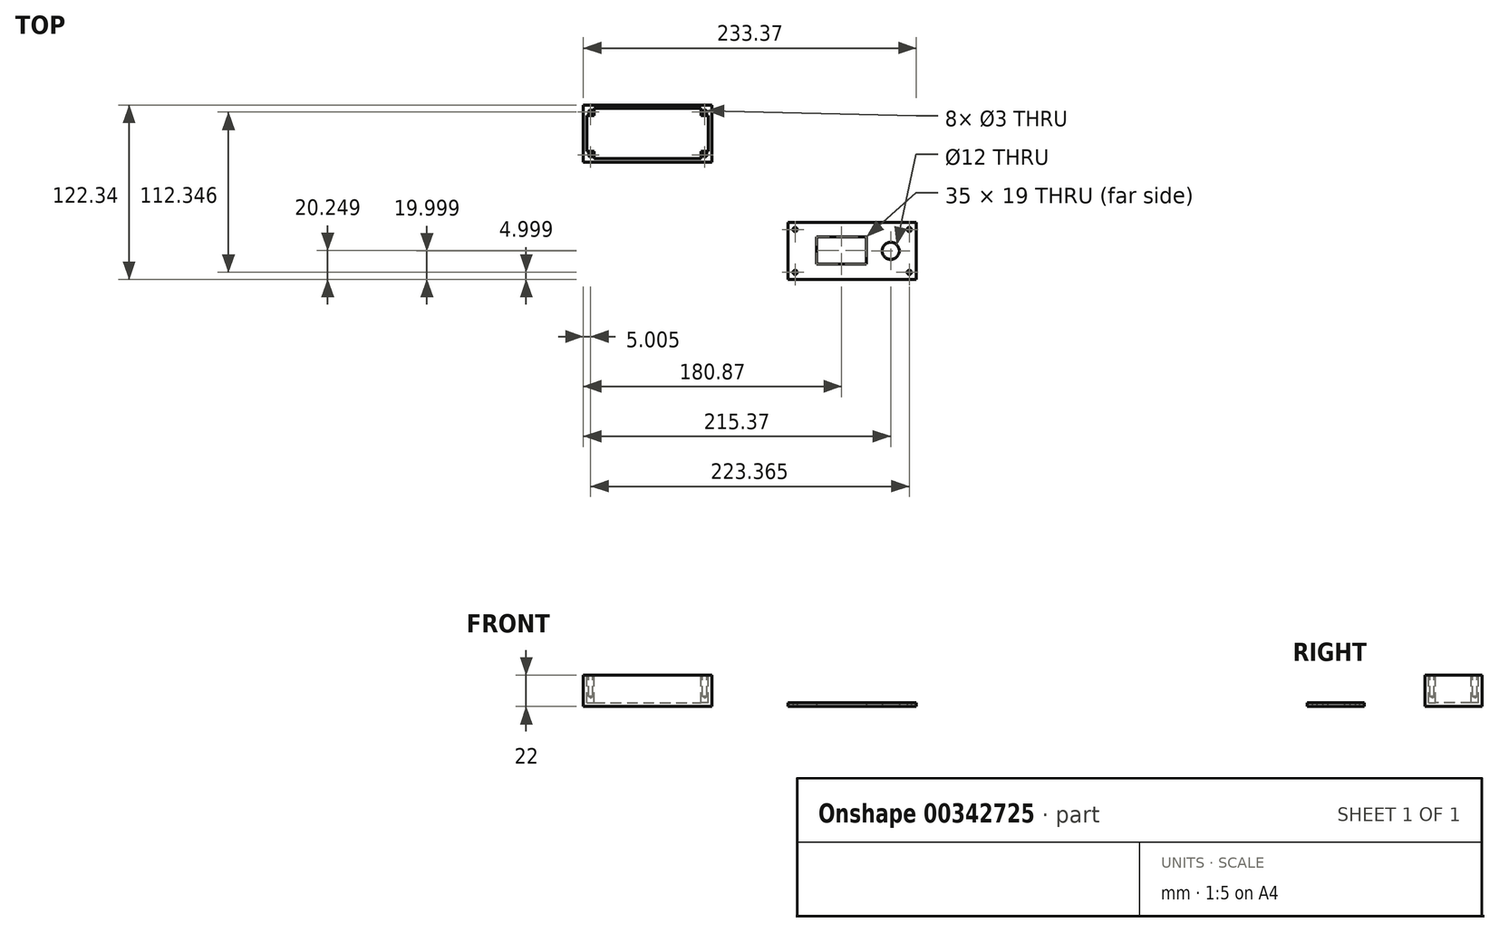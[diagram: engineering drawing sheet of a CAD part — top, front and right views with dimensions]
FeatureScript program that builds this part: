
annotation { "Feature Type Name" : "Feature", "Feature Type Description" : "" }
export const myFeature = defineFeature(function(context is Context, id is Id, definition is map)
    precondition{}
    {
        {
            var Q0;
            Q0=qCreatedBy(makeId("Top.planeOp"),FACE);
            var sketch = newSketch(context, id + "F0", { "sketchPlane" : qUnion([Q0])});
            skLineSegment(sketch, "E0.bottom", {"start": v(-186.8, 103.04) * mm, "end": v(-96.8, 103.04) * mm});
            skLineSegment(sketch, "E0.top", {"start": v(-186.8, 63.04) * mm, "end": v(-96.8, 63.04) * mm});
            skLineSegment(sketch, "E0.left", {"start": v(-186.8, 103.04) * mm, "end": v(-186.8, 63.04) * mm});
            skLineSegment(sketch, "E0.right", {"start": v(-96.8, 103.04) * mm, "end": v(-96.8, 63.04) * mm});
            skSolve(sketch);
        }
        {
            var Q0;
            Q0=makeQuery(id+"F0.imprint","IMPRINT",FACE,{"disambiguationData":[TD([[makeQuery(id+"F0.imprint","IMPRINT",EDGE,{"derivedFrom":sQuery(id+"F0.wireOp",EDGE,"E0.bottom")}),-1.0]])]});
            extrude(context, id + "F1", {"entities" : qUnion([Q0]), "depth" : 22 * mm});
        }
        {
            var Q0;
            Q0=makeQuery(id+"F1.opExtrude","CAP_FACE",FACE,{"disambiguationData":[OSD([sQuery(id+"F0.wireOp",EDGE,"E0.bottom"),sQuery(id+"F0.wireOp",EDGE,"E0.top"),sQuery(id+"F0.wireOp",EDGE,"E0.left"),sQuery(id+"F0.wireOp",EDGE,"E0.right")])],"isStart":false});
            shell(context, id + "F2", {"entities" : qUnion([Q0]), "thickness" : 2.5 * mm});
        }
        {
            var Q0;
            Q0=qCreatedBy(makeId("Top.planeOp"),FACE);
            var sketch = newSketch(context, id + "F3", { "sketchPlane" : qUnion([Q0])});
            skLineSegment(sketch, "E1.bottom", {"start": v(-43.44, 20.7) * mm, "end": v(46.56, 20.7) * mm});
            skLineSegment(sketch, "E1.top", {"start": v(-43.44, -19.3) * mm, "end": v(46.56, -19.3) * mm});
            skLineSegment(sketch, "E1.left", {"start": v(-43.44, 20.7) * mm, "end": v(-43.44, -19.3) * mm});
            skLineSegment(sketch, "E1.right", {"start": v(46.56, 20.7) * mm, "end": v(46.56, -19.3) * mm});
            skLineSegment(sketch, "E2.bottom", {"start": v(11.56, -8.55) * mm, "end": v(-23.44, -8.55) * mm});
            skLineSegment(sketch, "E2.top", {"start": v(11.56, 10.45) * mm, "end": v(-23.44, 10.45) * mm});
            skLineSegment(sketch, "E2.left", {"start": v(11.56, -8.55) * mm, "end": v(11.56, 10.45) * mm});
            skLineSegment(sketch, "E2.right", {"start": v(-23.44, -8.55) * mm, "end": v(-23.44, 10.45) * mm});
            skPoint(sketch, "E2.middle", {"position": v(-5.94, 0.95) * mm});
            skPoint(sketch, "E3", {"position": v(20.67, 0.11) * mm});
            skCircle(sketch, "E4", {"center": v(41.56, 15.7) * mm, "radius": 1.5 * mm});
            skCircle(sketch, "E5", {"center": v(41.56, -14.3) * mm, "radius": 1.5 * mm});
            skCircle(sketch, "E6", {"center": v(-38.44, 15.7) * mm, "radius": 1.5 * mm});
            skCircle(sketch, "E7", {"center": v(-38.44, -14.3) * mm, "radius": 1.5 * mm});
            skSolve(sketch);
        }
        {
            var Q0;
            Q0=makeQuery(id+"F3.imprint","IMPRINT",FACE,{"disambiguationData":[TD([[makeQuery(id+"F3.imprint","IMPRINT",EDGE,{"derivedFrom":sQuery(id+"F3.wireOp",EDGE,"E1.bottom")}),-1.0]])]});
            extrude(context, id + "F4", {"entities" : qUnion([Q0]), "depth" : 2.5 * mm});
        }
        {
            var Q0;
            Q0=makeQuery(id+"F3.imprint","IMPRINT",FACE,{"disambiguationData":[TD([[makeQuery(id+"F3.imprint","IMPRINT",EDGE,{"derivedFrom":sQuery(id+"F3.wireOp",EDGE,"E1.bottom")}),-1.0]])]});
            var sketch = newSketch(context, id + "F5", { "sketchPlane" : qUnion([Q0])});
            skCircle(sketch, "E8", {"center": v(28.56, 0.7) * mm, "radius": 6 * mm});
            skSolve(sketch);
        }
        {
            var Q0;
            Q0=makeQuery(id+"F5.imprint","IMPRINT",FACE,{"disambiguationData":[TD([[makeQuery(id+"F5.imprint","IMPRINT",EDGE,{"derivedFrom":sQuery(id+"F5.wireOp",EDGE,"E8")}),1.0]])]});
            extrude(context, id + "F6", {"entities" : qUnion([Q0]), "operationType" : NewBodyOperationType.REMOVE, "depth" : 25 * mm});
        }
        {
            var Q0;
            Q0=makeQuery(id+"F1.opExtrude","CAP_FACE",FACE,{"disambiguationData":[OSD([sQuery(id+"F0.wireOp",EDGE,"E0.bottom"),sQuery(id+"F0.wireOp",EDGE,"E0.top"),sQuery(id+"F0.wireOp",EDGE,"E0.left"),sQuery(id+"F0.wireOp",EDGE,"E0.right")])],"isStart":false});
            var sketch = newSketch(context, id + "F7", { "sketchPlane" : qUnion([Q0])});
            skLineSegment(sketch, "E9.bottom", {"start": v(-184.3, 95.54) * mm, "end": v(-179.3, 95.54) * mm});
            skLineSegment(sketch, "E9.top", {"start": v(-184.3, 100.54) * mm, "end": v(-179.3, 100.54) * mm});
            skLineSegment(sketch, "E9.left", {"start": v(-184.3, 95.54) * mm, "end": v(-184.3, 100.54) * mm});
            skLineSegment(sketch, "E9.right", {"start": v(-179.3, 95.54) * mm, "end": v(-179.3, 100.54) * mm});
            skLineSegment(sketch, "E10.bottom", {"start": v(-184.3, 65.54) * mm, "end": v(-179.3, 65.54) * mm});
            skLineSegment(sketch, "E10.top", {"start": v(-184.3, 70.54) * mm, "end": v(-179.3, 70.54) * mm});
            skLineSegment(sketch, "E10.left", {"start": v(-184.3, 65.54) * mm, "end": v(-184.3, 70.54) * mm});
            skLineSegment(sketch, "E10.right", {"start": v(-179.3, 65.54) * mm, "end": v(-179.3, 70.54) * mm});
            skLineSegment(sketch, "E11.bottom", {"start": v(-99.3, 100.54) * mm, "end": v(-104.3, 100.54) * mm});
            skLineSegment(sketch, "E11.top", {"start": v(-99.3, 95.54) * mm, "end": v(-104.3, 95.54) * mm});
            skLineSegment(sketch, "E11.left", {"start": v(-99.3, 100.54) * mm, "end": v(-99.3, 95.54) * mm});
            skLineSegment(sketch, "E11.right", {"start": v(-104.3, 100.54) * mm, "end": v(-104.3, 95.54) * mm});
            skLineSegment(sketch, "E12.bottom", {"start": v(-99.3, 65.54) * mm, "end": v(-104.3, 65.54) * mm});
            skLineSegment(sketch, "E12.top", {"start": v(-99.3, 70.54) * mm, "end": v(-104.3, 70.54) * mm});
            skLineSegment(sketch, "E12.left", {"start": v(-99.3, 65.54) * mm, "end": v(-99.3, 70.54) * mm});
            skLineSegment(sketch, "E12.right", {"start": v(-104.3, 65.54) * mm, "end": v(-104.3, 70.54) * mm});
            skPoint(sketch, "E13", {"position": v(-181.8, 98.04) * mm});
            skPoint(sketch, "E14", {"position": v(-181.8, 68.04) * mm});
            skPoint(sketch, "E15", {"position": v(-101.8, 68.04) * mm});
            skPoint(sketch, "E16", {"position": v(-101.8, 98.04) * mm});
            skSolve(sketch);
        }
        {
            var Q0;
            Q0=makeQuery(id+"F7.imprint","IMPRINT",FACE,{"disambiguationData":[TD([[makeQuery(id+"F7.imprint","IMPRINT",EDGE,{"derivedFrom":sQuery(id+"F7.wireOp",EDGE,"E9.bottom")}),1.0]])]});
            var Q1;
            Q1=makeQuery(id+"F7.imprint","IMPRINT",FACE,{"disambiguationData":[TD([[makeQuery(id+"F7.imprint","IMPRINT",EDGE,{"derivedFrom":sQuery(id+"F7.wireOp",EDGE,"E11.bottom")}),-1.0]])]});
            var Q2;
            Q2=makeQuery(id+"F7.imprint","IMPRINT",FACE,{"disambiguationData":[TD([[makeQuery(id+"F7.imprint","IMPRINT",EDGE,{"derivedFrom":sQuery(id+"F7.wireOp",EDGE,"E12.bottom")}),1.0]])]});
            var Q3;
            Q3=makeQuery(id+"F7.imprint","IMPRINT",FACE,{"disambiguationData":[TD([[makeQuery(id+"F7.imprint","IMPRINT",EDGE,{"derivedFrom":sQuery(id+"F7.wireOp",EDGE,"E10.bottom")}),1.0]])]});
            extrude(context, id + "F8", {"entities" : qUnion([Q0, Q1, Q2, Q3]), "operationType" : NewBodyOperationType.ADD, "oppositeDirection" : true, "depth" : 22 * mm});
        }
        {
            var Q0;
            Q0=sQuery(id+"F7.wireOp",VERTEX,"E13");
            var Q1;
            Q1=sQuery(id+"F7.wireOp",VERTEX,"E14");
            var Q2;
            Q2=sQuery(id+"F7.wireOp",VERTEX,"E16");
            var Q3;
            Q3=sQuery(id+"F7.wireOp",VERTEX,"E15");
            var Q4;
            Q4=makeQuery(id+"F1.opExtrude","SWEPT_BODY",BODY,{"disambiguationData":[OSD([sQuery(id+"F0.wireOp",EDGE,"E0.bottom"),sQuery(id+"F0.wireOp",EDGE,"E0.top"),sQuery(id+"F0.wireOp",EDGE,"E0.left"),sQuery(id+"F0.wireOp",EDGE,"E0.right")])]});
            hole(context, id + "F9", {"style" : HoleStyle.SIMPLE, "endStyle" : HoleEndStyle.BLIND, "holeDiameter" : 3 * mm, "holeDepth" : 15 * mm, "isTappedThrough" : true, "tappedDepth" : 12 * mm, "tapClearance" : 3, "startFromSketch" : true, "locations" : qUnion([Q0, Q1, Q2, Q3]), "scope" : qUnion([Q4])});
        }
    });
